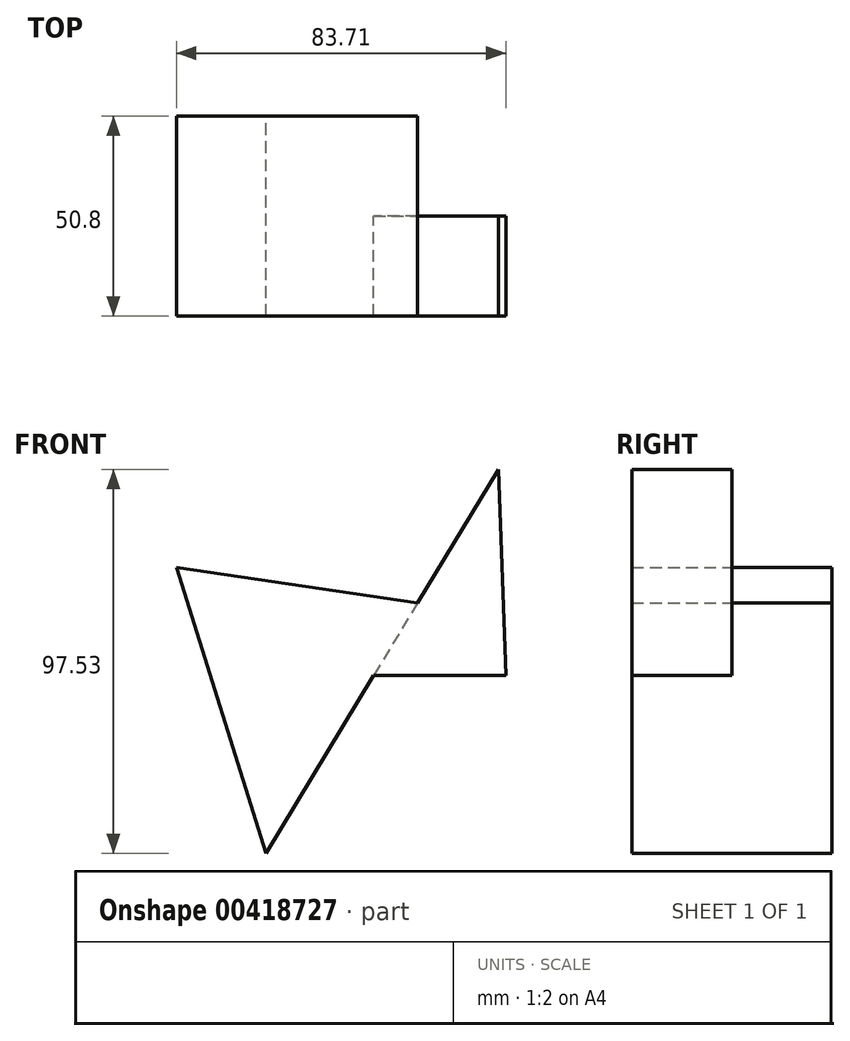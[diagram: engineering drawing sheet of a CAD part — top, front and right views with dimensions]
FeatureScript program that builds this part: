
annotation { "Feature Type Name" : "Feature", "Feature Type Description" : "" }
export const myFeature = defineFeature(function(context is Context, id is Id, definition is map)
    precondition{}
    {
        {
            var Q0;
            Q0=qCreatedBy(makeId("Front.planeOp"),FACE);
            var sketch = newSketch(context, id + "F0", { "sketchPlane" : qUnion([Q0])});
            skLineSegment(sketch, "E0", {"start": v(0, 0) * mm, "end": v(31.73, 0) * mm});
            skLineSegment(sketch, "E1", {"start": v(31.73, 0) * mm, "end": v(53.92, 0) * mm});
            skLineSegment(sketch, "E2", {"start": v(0, 0) * mm, "end": v(57.62, 0) * mm});
            skLineSegment(sketch, "E3", {"start": v(57.62, 0) * mm, "end": v(55.68, 52.37) * mm});
            skLineSegment(sketch, "E4", {"start": v(55.68, 52.37) * mm, "end": v(-3.3, -45.16) * mm});
            skLineSegment(sketch, "E5", {"start": v(-3.3, -45.16) * mm, "end": v(-26.09, 27.45) * mm});
            skLineSegment(sketch, "E6", {"start": v(-26.09, 27.45) * mm, "end": v(61.71, 14.6) * mm});
            skSolve(sketch);
        }
        {
            var Q0;
            {var subQ4=sQuery(id+"F0.wireOp",EDGE,"E5");Q0=makeQuery(id+"F0.imprint","IMPRINT",FACE,{"disambiguationData":[TD([[makeQuery(id+"F0.imprint","IMPRINT",EDGE,{"derivedFrom":subQ4}),-1.0]])]});}
            extrude(context, id + "F1", {"entities" : qUnion([Q0]), "depth" : 25.4 * mm, "hasSecondDirection" : true, "secondDirectionOppositeDirection" : true, "secondDirectionDepth" : 25.4 * mm});
        }
        {
            var Q0;
            Q0 = qSketchRegion(id + "F0", true);
            extrude(context, id + "F2", {"entities" : qUnion([Q0]), "operationType" : NewBodyOperationType.ADD, "depth" : 25.4 * mm});
        }
    });
